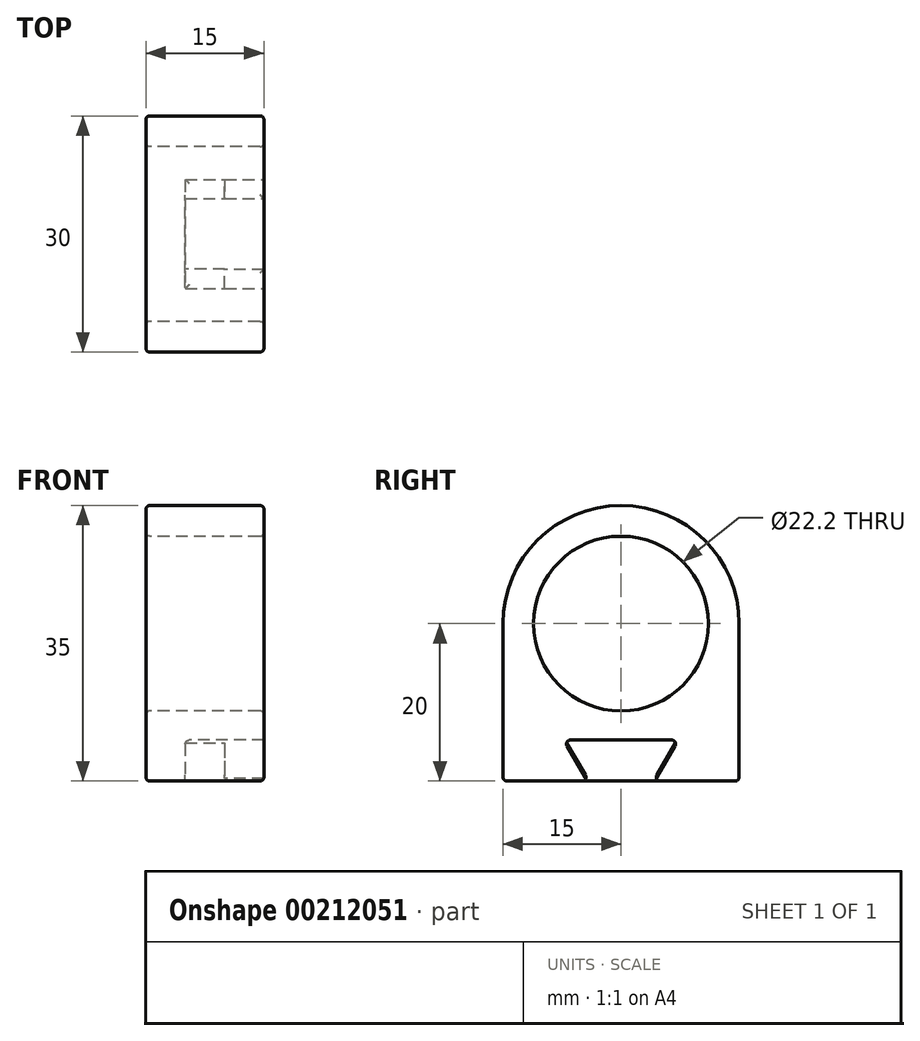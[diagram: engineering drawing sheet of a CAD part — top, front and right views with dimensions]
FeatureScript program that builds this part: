
annotation { "Feature Type Name" : "Feature", "Feature Type Description" : "" }
export const myFeature = defineFeature(function(context is Context, id is Id, definition is map)
    precondition{}
    {
        {
            var Q0;
            Q0=qCreatedBy(makeId("Front.planeOp"),FACE);
            var sketch = newSketch(context, id + "F0", { "sketchPlane" : qUnion([Q0])});
            skLineSegment(sketch, "E0.top", {"start": v(0, 15) * mm, "end": v(15, 15) * mm});
            skLineSegment(sketch, "E1.top", {"start": v(0, 11.1) * mm, "end": v(15, 11.1) * mm});
            skLineSegment(sketch, "E1.left", {"start": v(0, 15) * mm, "end": v(0, 11.1) * mm});
            skLineSegment(sketch, "E1.right", {"start": v(15, 15) * mm, "end": v(15, 11.1) * mm});
            skSolve(sketch);
        }
        {
            var Q0;
            Q0=qCreatedBy(makeId("Front.planeOp"),FACE);
            var sketch = newSketch(context, id + "F1", { "sketchPlane" : qUnion([Q0])});
            skLineSegment(sketch, "E2", {"start": v(0, 0) * mm, "end": v(22.57, 0) * mm});
            skSolve(sketch);
        }
        {
            var Q0;
            Q0=makeQuery(id+"F0.imprint","IMPRINT",FACE,{"disambiguationData":[TD([[makeQuery(id+"F0.imprint","IMPRINT",EDGE,{"derivedFrom":sQuery(id+"F0.wireOp",EDGE,"E0.top")}),-1.0]])]});
            var Q1;
            Q1=sQuery(id+"F1.wireOp",EDGE,"E2");
            revolve(context, id + "F2", {"entities" : qUnion([Q0]), "axis" : qUnion([Q1]), "revolveType" : RevolveType.FULL});
        }
        {
            var Q0;
            Q0=qCreatedBy(makeId("Right.planeOp"),FACE);
            var sketch = newSketch(context, id + "F3", { "sketchPlane" : qUnion([Q0])});
            skArc(sketch, "E3", {"start": v(-15, 0) * mm, "mid": v(0, -15) * mm, "end": v(15, 0) * mm});
            skLineSegment(sketch, "E4", {"start": v(-15, 0) * mm, "end": v(-15, -20) * mm});
            skLineSegment(sketch, "E5", {"start": v(15, 0) * mm, "end": v(15, -20) * mm});
            skLineSegment(sketch, "E6", {"start": v(15, -20) * mm, "end": v(-15, -20) * mm});
            skSolve(sketch);
        }
        {
            var Q0;
            Q0=qSketchRegion(id+"F3",true);
            extrude(context, id + "F4", {"entities" : qUnion([Q0]), "operationType" : NewBodyOperationType.ADD, "depth" : 15 * mm});
        }
        {
            var Q0;
            Q0=qCreatedBy(makeId("Right.planeOp"),FACE);
            var sketch = newSketch(context, id + "F5", { "sketchPlane" : qUnion([Q0])});
            skLineSegment(sketch, "E7", {"start": v(-4.3, -20) * mm, "end": v(4.3, -20) * mm});
            skLineSegment(sketch, "E8", {"start": v(4.3, -20) * mm, "end": v(7.3, -14.8) * mm});
            skLineSegment(sketch, "E9", {"start": v(7.3, -14.8) * mm, "end": v(-7.3, -14.8) * mm});
            skLineSegment(sketch, "E10", {"start": v(-7.3, -14.8) * mm, "end": v(-4.3, -20) * mm});
            skSolve(sketch);
        }
        {
            var Q0;
            Q0=qSketchRegion(id+"F5",true);
            extrude(context, id + "F6", {"entities" : qUnion([Q0]), "operationType" : NewBodyOperationType.REMOVE, "depth" : 15 * mm, "hasSecondDirection" : true, "secondDirectionOppositeDirection" : false, "secondDirectionDepth" : 5 * mm});
        }
        {
            var Q0;
            Q0=makeQuery(id+"F6.boolean.opBoolean","COPY",FACE,{"derivedFrom":makeQuery(id+"F6.opExtrude","CAP_FACE",FACE,{"disambiguationData":[OSD([sQuery(id+"F5.wireOp",EDGE,"E7"),sQuery(id+"F5.wireOp",EDGE,"E8"),sQuery(id+"F5.wireOp",EDGE,"E9"),sQuery(id+"F5.wireOp",EDGE,"E10")])],"isStart":true})});
            var sketch = newSketch(context, id + "F7", { "sketchPlane" : qUnion([Q0])});
            skLineSegment(sketch, "E11", {"start": v(-7.3, -14.8) * mm, "end": v(-7.1, -14.8) * mm});
            skLineSegment(sketch, "E12", {"start": v(-7.1, -14.8) * mm, "end": v(-4.1, -20) * mm});
            skLineSegment(sketch, "E13", {"start": v(-4.1, -20) * mm, "end": v(-4.3, -20) * mm});
            skLineSegment(sketch, "E14", {"start": v(-4.3, -20) * mm, "end": v(-7.3, -14.8) * mm});
            skLineSegment(sketch, "E15", {"start": v(7.3, -14.8) * mm, "end": v(7.1, -14.8) * mm});
            skLineSegment(sketch, "E16", {"start": v(7.1, -14.8) * mm, "end": v(4.1, -20) * mm});
            skLineSegment(sketch, "E17", {"start": v(4.1, -20) * mm, "end": v(4.3, -20) * mm});
            skLineSegment(sketch, "E18", {"start": v(4.3, -20) * mm, "end": v(7.3, -14.8) * mm});
            skSolve(sketch);
        }
        {
            var Q0;
            Q0=qSketchRegion(id+"F7",true);
            extrude(context, id + "F8", {"entities" : qUnion([Q0]), "operationType" : NewBodyOperationType.ADD, "depth" : 5 * mm});
        }
        {
            var Q0;
            Q0=makeQuery(id+"F2.opRevolve","SWEPT_EDGE",EDGE,{"disambiguationData":[OSD([sQuery(id+"F0.wireOp",EDGE,"E0.top"),sQuery(id+"F0.wireOp",EDGE,"1lQ0kiGw-1SfZ-g20Q-AWwg-a69r1B9lKGPj")])]});
            var Q1;
            Q1=makeQuery(id+"F2.opRevolve","SWEPT_EDGE",EDGE,{"disambiguationData":[OSD([sQuery(id+"F0.wireOp",EDGE,"E0.top"),sQuery(id+"F0.wireOp",EDGE,"pjw5n2tj-4ZJl-OT3E-6ASZ-qqbg0eeyxjkH")])]});
            var Q2;
            Q2=makeQuery(id+"F4.opExtrude","CAP_EDGE",EDGE,{"disambiguationData":[OSD([sQuery(id+"F3.wireOp",EDGE,"E6")])],"isStart":false});
            var Q3;
            Q3=makeQuery(id+"F4.opExtrude","SWEPT_EDGE",EDGE,{"disambiguationData":[OSD([sQuery(id+"F3.wireOp",EDGE,"E4"),sQuery(id+"F3.wireOp",EDGE,"E6")])]});
            var Q4;
            Q4=makeQuery(id+"F4.opExtrude","CAP_EDGE",EDGE,{"disambiguationData":[OSD([sQuery(id+"F3.wireOp",EDGE,"E6")])],"isStart":true});
            var Q5;
            Q5=makeQuery(id+"F4.opExtrude","SWEPT_EDGE",EDGE,{"disambiguationData":[OSD([sQuery(id+"F3.wireOp",EDGE,"E5"),sQuery(id+"F3.wireOp",EDGE,"E6")])]});
            var Q6;
            Q6=makeQuery(id+"F8.opExtrude","SWEPT_EDGE",EDGE,{"disambiguationData":[OSD([sQuery(id+"F5.wireOp",EDGE,"E7"),sQuery(id+"F7.wireOp",EDGE,"E12"),sQuery(id+"F7.wireOp",EDGE,"E13")])]});
            var Q7;
            Q7=makeQuery(id+"F6.boolean.opBoolean","COPY",EDGE,{"derivedFrom":makeQuery(id+"F6.opExtrude","CAP_EDGE",EDGE,{"disambiguationData":[OSD([sQuery(id+"F5.wireOp",EDGE,"E7")])],"isStart":true})});
            var Q8;
            Q8=makeQuery(id+"F8.opExtrude","SWEPT_EDGE",EDGE,{"disambiguationData":[OSD([sQuery(id+"F5.wireOp",EDGE,"E7"),sQuery(id+"F7.wireOp",EDGE,"E16"),sQuery(id+"F7.wireOp",EDGE,"E17")])]});
            var Q9;
            Q9=makeQuery(id+"F6.boolean.opBoolean","COPY",EDGE,{"derivedFrom":makeQuery(id+"F6.opExtrude","CAP_EDGE",EDGE,{"disambiguationData":[OSD([sQuery(id+"F5.wireOp",EDGE,"E8")])],"isStart":false})});
            var Q10;
            Q10=makeQuery(id+"F6.boolean.opBoolean","COPY",EDGE,{"derivedFrom":makeQuery(id+"F6.opExtrude","CAP_EDGE",EDGE,{"disambiguationData":[OSD([sQuery(id+"F5.wireOp",EDGE,"E9")])],"isStart":false})});
            var Q11;
            Q11=makeQuery(id+"F6.boolean.opBoolean","COPY",EDGE,{"derivedFrom":makeQuery(id+"F6.opExtrude","CAP_EDGE",EDGE,{"disambiguationData":[OSD([sQuery(id+"F5.wireOp",EDGE,"E10")])],"isStart":false})});
            var Q12;
            Q12=makeQuery(id+"F6.boolean.opBoolean","COPY",EDGE,{"derivedFrom":makeQuery(id+"F6.opExtrude","SWEPT_EDGE",EDGE,{"disambiguationData":[OSD([sQuery(id+"F5.wireOp",EDGE,"E8"),sQuery(id+"F5.wireOp",EDGE,"E9")])]})});
            var Q13;
            Q13=makeQuery(id+"F6.boolean.opBoolean","COPY",EDGE,{"derivedFrom":makeQuery(id+"F6.opExtrude","SWEPT_EDGE",EDGE,{"disambiguationData":[OSD([sQuery(id+"F5.wireOp",EDGE,"E9"),sQuery(id+"F5.wireOp",EDGE,"E10")])]})});
            var Q14;
            Q14=makeQuery(id+"F8.opExtrude","CAP_EDGE",EDGE,{"disambiguationData":[OSD([sQuery(id+"F7.wireOp",EDGE,"E12")])],"isStart":true});
            var Q15;
            Q15=makeQuery(id+"F6.boolean.opBoolean","COPY",EDGE,{"derivedFrom":makeQuery(id+"F6.opExtrude","CAP_EDGE",EDGE,{"disambiguationData":[OSD([sQuery(id+"F5.wireOp",EDGE,"E9")])],"isStart":true})});
            var Q16;
            Q16=makeQuery(id+"F8.opExtrude","CAP_EDGE",EDGE,{"disambiguationData":[OSD([sQuery(id+"F7.wireOp",EDGE,"E16")])],"isStart":true});
            var Q17;
            Q17=makeQuery(id+"F2.opRevolve","SWEPT_EDGE",EDGE,{"disambiguationData":[OSD([sQuery(id+"F0.wireOp",EDGE,"E1.top"),sQuery(id+"F0.wireOp",EDGE,"E1.left")])]});
            var Q18;
            Q18=makeQuery(id+"F2.opRevolve","SWEPT_EDGE",EDGE,{"disambiguationData":[OSD([sQuery(id+"F0.wireOp",EDGE,"E1.top"),sQuery(id+"F0.wireOp",EDGE,"E1.right")])]});
            fillet(context, id + "F9", {"entities" : qUnion([Q0, Q1, Q2, Q3, Q4, Q5, Q6, Q7, Q8, Q9, Q10, Q11, Q12, Q13, Q14, Q15, Q16, Q17, Q18]), "radius" : 0.5 * mm, "tangentPropagation" : true, "allowEdgeOverflow" : false});
        }
    });
